# Revit family: Faucet-Bedpan_Washer-Zurn-Z877P2-LKS-HK-SH2
name_source: partatom
category: Plumbing Fixtures
units: mm (PartAtom-declared; Revit-internal decimal feet)

## family parameters
Cut with Voids When Loaded = No
Host = Face
Maintain Annotation Orientation = No
OmniClass Number = 23.45.55.14
OmniClass Title = Single Faucets
Part Type = Normal
Room Calculation Point = No
Round Connector Dimension = Use Radius
Shared = No

## types (1)
- Z877P2-LKS-HK-SH2 (AquaSpec® Bedpan Washer)
    Activation Method = Manually Operated
    Assembly Code = D2010.60
    CW Connection = Yes
    CWFU = 0
    Default Elevation = 48 "
    Description = AquaSpec® Bedpan Washer
    HW Connection = No
    HWFU = 0
    Inlet Connection Size = 1.5 "
    Installtion Height from Ground = 64 "
    Main Material = Chrome-Plated Brass - Zurn - Polished
    Manufacturer = Zurn Water, LLC
    Manufacturer Brand = Zurn
    Mode of Installation = Wall Mounted
    Model = Z877P2-LKS-HK-SH2
    Modified Date = 07/16/2025
    Product Page URL = https://www.zurn.com
    Product data URL = https://www.bimobject.com
    Repair Parts URL = https://files.zurn.com
    Spout Height = 4.25 "
    Spout Reach = 5.625 "
    Spout location from Wall = 4.25 "
    Type of Handle = Four Arm Vandal Resistant Color Coded Lever Handles
    URL = https://www.zurn.com
    Vent Connection = No
    Vinly Hose Length = 48 "
    WFU = 0
    Waste Connection = No

## geometry (parser evidence)
native form markers: Sweep x4
no freeform markers — native parametric forms only
